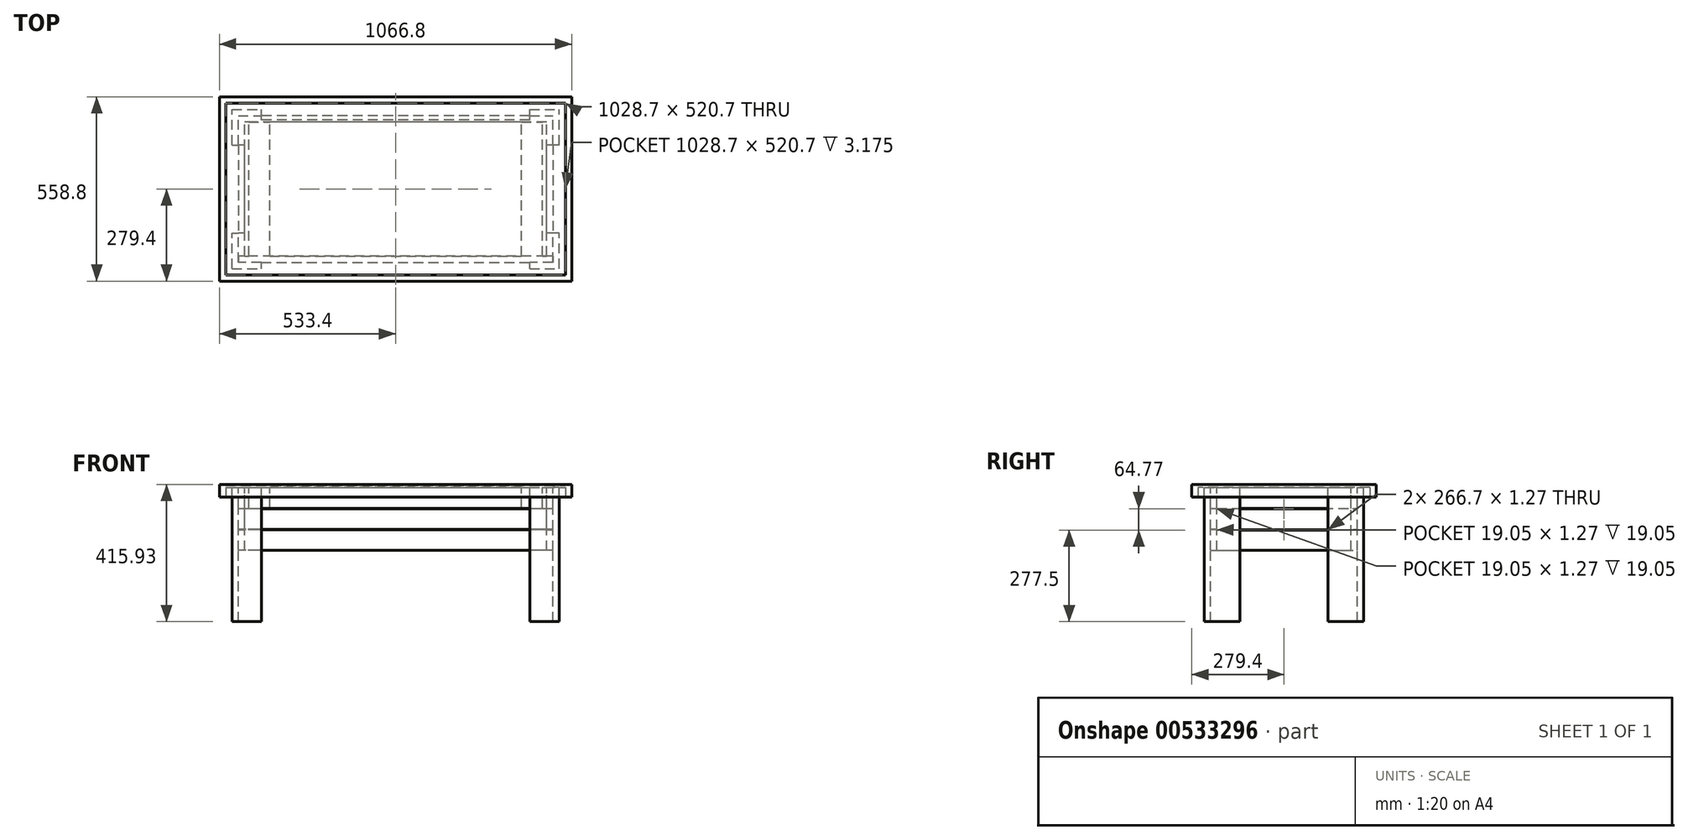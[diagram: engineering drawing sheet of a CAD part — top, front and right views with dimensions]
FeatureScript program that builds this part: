
annotation { "Feature Type Name" : "Feature", "Feature Type Description" : "" }
export const myFeature = defineFeature(function(context is Context, id is Id, definition is map)
    precondition{}
    {
        {
            var Q0;
            Q0=qCreatedBy(makeId("Top.planeOp"),FACE);
            var sketch = newSketch(context, id + "F0", { "sketchPlane" : qUnion([Q0])});
            skLineSegment(sketch, "E0.bottom", {"start": v(-533.4, -279.4) * mm, "end": v(533.4, -279.4) * mm});
            skLineSegment(sketch, "E0.top", {"start": v(-533.4, 279.4) * mm, "end": v(533.4, 279.4) * mm});
            skLineSegment(sketch, "E0.left", {"start": v(-533.4, -279.4) * mm, "end": v(-533.4, 279.4) * mm});
            skLineSegment(sketch, "E0.right", {"start": v(533.4, -279.4) * mm, "end": v(533.4, 279.4) * mm});
            skPoint(sketch, "E0.middle", {"position": v(0, 0) * mm});
            skLineSegment(sketch, "E1.bottom", {"start": v(-514.35, -260.35) * mm, "end": v(514.35, -260.35) * mm});
            skLineSegment(sketch, "E1.top", {"start": v(-514.35, 260.35) * mm, "end": v(514.35, 260.35) * mm});
            skLineSegment(sketch, "E1.left", {"start": v(-514.35, -260.35) * mm, "end": v(-514.35, 260.35) * mm});
            skLineSegment(sketch, "E1.right", {"start": v(514.35, -260.35) * mm, "end": v(514.35, 260.35) * mm});
            skSolve(sketch);
        }
        {
            var Q0;
            Q0=makeQuery(id+"F0.imprint","IMPRINT",FACE,{"disambiguationData":[TD([[makeQuery(id+"F0.imprint","IMPRINT",EDGE,{"derivedFrom":sQuery(id+"F0.wireOp",EDGE,"E0.bottom")}),1.0]])]});
            extrude(context, id + "F1", {"entities" : qUnion([Q0]), "depth" : 38.1 * mm, "offsetDistance" : 25.4 * mm});
        }
        {
            var Q0;
            Q0=makeQuery(id+"F1.opExtrude","SWEPT_FACE",FACE,{"disambiguationData":[OSD([sQuery(id+"F0.wireOp",EDGE,"E1.bottom")])]});
            var sketch = newSketch(context, id + "F2", { "sketchPlane" : qUnion([Q0])});
            skLineSegment(sketch, "E2.bottom", {"start": v(514.35, 34.93) * mm, "end": v(-514.35, 34.92) * mm});
            skLineSegment(sketch, "E2.top", {"start": v(514.35, 28.58) * mm, "end": v(-514.35, 28.57) * mm});
            skLineSegment(sketch, "E2.left", {"start": v(514.35, 34.93) * mm, "end": v(514.35, 28.58) * mm});
            skLineSegment(sketch, "E2.right", {"start": v(-514.35, 34.92) * mm, "end": v(-514.35, 28.57) * mm});
            skSolve(sketch);
        }
        {
            var Q0;
            Q0 = qSketchRegion(id + "F2", true);
            extrude(context, id + "F3", {"entities" : qUnion([Q0]), "operationType" : NewBodyOperationType.ADD, "depth" : 520.7 * mm, "offsetDistance" : 25.4 * mm});
        }
        {
            var Q0;
            Q0=makeQuery(id+"F3.opExtrude","SWEPT_FACE",FACE,{"disambiguationData":[OSD([sQuery(id+"F2.wireOp",EDGE,"E2.top")])]});
            var sketch = newSketch(context, id + "F4", { "sketchPlane" : qUnion([Q0])});
            skLineSegment(sketch, "E3.bottom", {"start": v(-476.25, 222.25) * mm, "end": v(476.25, 222.25) * mm});
            skLineSegment(sketch, "E3.top", {"start": v(-476.25, 203.2) * mm, "end": v(476.25, 203.2) * mm});
            skLineSegment(sketch, "E3.left", {"start": v(-476.25, 222.25) * mm, "end": v(-476.25, 203.2) * mm});
            skLineSegment(sketch, "E3.right", {"start": v(476.25, 222.25) * mm, "end": v(476.25, 203.2) * mm});
            skSolve(sketch);
        }
        {
            var Q0;
            Q0=makeQuery(id+"F4.imprint","IMPRINT",FACE,{"disambiguationData":[TD([[makeQuery(id+"F4.imprint","IMPRINT",EDGE,{"derivedFrom":sQuery(id+"F4.wireOp",EDGE,"E3.bottom")}),-1.0]])]});
            extrude(context, id + "F5", {"entities" : qUnion([Q0]), "operationType" : NewBodyOperationType.ADD, "depth" : 63.5 * mm, "offsetDistance" : 25.4 * mm});
        }
        {
            var Q0;
            Q0=makeQuery(id+"F3.opExtrude","SWEPT_FACE",FACE,{"disambiguationData":[OSD([sQuery(id+"F2.wireOp",EDGE,"E2.top")])]});
            var sketch = newSketch(context, id + "F6", { "sketchPlane" : qUnion([Q0])});
            skLineSegment(sketch, "E4.bottom", {"start": v(-444.5, 203.2) * mm, "end": v(-381, 203.2) * mm});
            skLineSegment(sketch, "E4.top", {"start": v(-444.5, -203.2) * mm, "end": v(-381, -203.2) * mm});
            skLineSegment(sketch, "E4.left", {"start": v(-444.5, 203.2) * mm, "end": v(-444.5, -203.2) * mm});
            skLineSegment(sketch, "E4.right", {"start": v(-381, 203.2) * mm, "end": v(-381, -203.2) * mm});
            skLineSegment(sketch, "E5.bottom", {"start": v(381, 203.2) * mm, "end": v(444.5, 203.2) * mm});
            skLineSegment(sketch, "E5.top", {"start": v(381, -203.2) * mm, "end": v(444.5, -203.2) * mm});
            skLineSegment(sketch, "E5.left", {"start": v(381, 203.2) * mm, "end": v(381, -203.2) * mm});
            skLineSegment(sketch, "E5.right", {"start": v(444.5, 203.2) * mm, "end": v(444.5, -203.2) * mm});
            skSolve(sketch);
        }
        {
            var Q0;
            Q0 = qSketchRegion(id + "F6", true);
            extrude(context, id + "F7", {"entities" : qUnion([Q0]), "operationType" : NewBodyOperationType.ADD, "depth" : 63.5 * mm, "offsetDistance" : 25.4 * mm});
        }
        {
            var Q0;
            Q0=makeQuery(id+"F3.opExtrude","SWEPT_FACE",FACE,{"disambiguationData":[OSD([sQuery(id+"F2.wireOp",EDGE,"E2.top")])]});
            var sketch = newSketch(context, id + "F8", { "sketchPlane" : qUnion([Q0])});
            skLineSegment(sketch, "E6.bottom", {"start": v(-495.3, 241.3) * mm, "end": v(-406.4, 241.3) * mm});
            skLineSegment(sketch, "E6.top", {"start": v(-495.3, 222.25) * mm, "end": v(-406.4, 222.25) * mm});
            skLineSegment(sketch, "E6.left", {"start": v(-495.3, 241.3) * mm, "end": v(-495.3, 222.25) * mm});
            skLineSegment(sketch, "E6.right", {"start": v(-406.4, 241.3) * mm, "end": v(-406.4, 222.25) * mm});
            skLineSegment(sketch, "E7.bottom", {"start": v(-495.3, -222.25) * mm, "end": v(-406.4, -222.25) * mm});
            skLineSegment(sketch, "E7.top", {"start": v(-495.3, -241.3) * mm, "end": v(-406.4, -241.3) * mm});
            skLineSegment(sketch, "E7.left", {"start": v(-495.3, -222.25) * mm, "end": v(-495.3, -241.3) * mm});
            skLineSegment(sketch, "E7.right", {"start": v(-406.4, -222.25) * mm, "end": v(-406.4, -241.3) * mm});
            skLineSegment(sketch, "E8.bottom", {"start": v(406.4, -222.25) * mm, "end": v(495.3, -222.25) * mm});
            skLineSegment(sketch, "E8.top", {"start": v(406.4, -241.3) * mm, "end": v(495.3, -241.3) * mm});
            skLineSegment(sketch, "E8.left", {"start": v(406.4, -222.25) * mm, "end": v(406.4, -241.3) * mm});
            skLineSegment(sketch, "E8.right", {"start": v(495.3, -222.25) * mm, "end": v(495.3, -241.3) * mm});
            skLineSegment(sketch, "E9.bottom", {"start": v(406.4, 241.3) * mm, "end": v(495.3, 241.3) * mm});
            skLineSegment(sketch, "E9.top", {"start": v(406.4, 222.25) * mm, "end": v(495.3, 222.25) * mm});
            skLineSegment(sketch, "E9.left", {"start": v(406.4, 241.3) * mm, "end": v(406.4, 222.25) * mm});
            skLineSegment(sketch, "E9.right", {"start": v(495.3, 241.3) * mm, "end": v(495.3, 222.25) * mm});
            skLineSegment(sketch, "E10.bottom", {"start": v(-495.3, 222.25) * mm, "end": v(-476.25, 222.25) * mm});
            skLineSegment(sketch, "E10.top", {"start": v(-495.3, 133.35) * mm, "end": v(-476.25, 133.35) * mm});
            skLineSegment(sketch, "E10.left", {"start": v(-495.3, 222.25) * mm, "end": v(-495.3, 133.35) * mm});
            skLineSegment(sketch, "E10.right", {"start": v(-476.25, 222.25) * mm, "end": v(-476.25, 133.35) * mm});
            skLineSegment(sketch, "E11.bottom", {"start": v(-495.3, -222.25) * mm, "end": v(-476.25, -222.25) * mm});
            skLineSegment(sketch, "E11.top", {"start": v(-495.3, -133.35) * mm, "end": v(-476.25, -133.35) * mm});
            skLineSegment(sketch, "E11.left", {"start": v(-495.3, -222.25) * mm, "end": v(-495.3, -133.35) * mm});
            skLineSegment(sketch, "E11.right", {"start": v(-476.25, -222.25) * mm, "end": v(-476.25, -133.35) * mm});
            skLineSegment(sketch, "E12.bottom", {"start": v(495.3, 222.25) * mm, "end": v(476.25, 222.25) * mm});
            skLineSegment(sketch, "E12.top", {"start": v(495.3, 133.35) * mm, "end": v(476.25, 133.35) * mm});
            skLineSegment(sketch, "E12.left", {"start": v(495.3, 222.25) * mm, "end": v(495.3, 133.35) * mm});
            skLineSegment(sketch, "E12.right", {"start": v(476.25, 222.25) * mm, "end": v(476.25, 133.35) * mm});
            skLineSegment(sketch, "E13.bottom", {"start": v(495.3, -222.25) * mm, "end": v(476.25, -222.25) * mm});
            skLineSegment(sketch, "E13.top", {"start": v(495.3, -133.35) * mm, "end": v(476.25, -133.35) * mm});
            skLineSegment(sketch, "E13.left", {"start": v(495.3, -222.25) * mm, "end": v(495.3, -133.35) * mm});
            skLineSegment(sketch, "E13.right", {"start": v(476.25, -222.25) * mm, "end": v(476.25, -133.35) * mm});
            skSolve(sketch);
        }
        {
            var Q0;
            Q0 = qSketchRegion(id + "F8", true);
            extrude(context, id + "F9", {"entities" : qUnion([Q0]), "operationType" : NewBodyOperationType.ADD, "depth" : 406.4 * mm, "offsetDistance" : 25.4 * mm});
        }
        {
            var Q0;
            Q0=makeQuery(id+"F3.opExtrude","SWEPT_FACE",FACE,{"disambiguationData":[OSD([sQuery(id+"F2.wireOp",EDGE,"E2.top")])]});
            var sketch = newSketch(context, id + "F10", { "sketchPlane" : qUnion([Q0])});
            skLineSegment(sketch, "E14.bottom", {"start": v(476.25, 203.2) * mm, "end": v(457.2, 203.2) * mm});
            skLineSegment(sketch, "E14.top", {"start": v(476.25, -222.25) * mm, "end": v(457.2, -222.25) * mm});
            skLineSegment(sketch, "E14.left", {"start": v(476.25, 203.2) * mm, "end": v(476.25, -222.25) * mm});
            skLineSegment(sketch, "E14.right", {"start": v(457.2, 203.2) * mm, "end": v(457.2, -222.25) * mm});
            skLineSegment(sketch, "E15.bottom", {"start": v(457.2, -222.25) * mm, "end": v(-457.2, -222.25) * mm});
            skLineSegment(sketch, "E15.top", {"start": v(457.2, -203.2) * mm, "end": v(-457.2, -203.2) * mm});
            skLineSegment(sketch, "E15.left", {"start": v(457.2, -222.25) * mm, "end": v(457.2, -203.2) * mm});
            skLineSegment(sketch, "E15.right", {"start": v(-457.2, -222.25) * mm, "end": v(-457.2, -203.2) * mm});
            skLineSegment(sketch, "E16.bottom", {"start": v(-476.25, 203.2) * mm, "end": v(-457.2, 203.2) * mm});
            skLineSegment(sketch, "E16.top", {"start": v(-476.25, -222.25) * mm, "end": v(-457.2, -222.25) * mm});
            skLineSegment(sketch, "E16.left", {"start": v(-476.25, 203.2) * mm, "end": v(-476.25, -222.25) * mm});
            skLineSegment(sketch, "E16.right", {"start": v(-457.2, 203.2) * mm, "end": v(-457.2, -222.25) * mm});
            skSolve(sketch);
        }
        {
            var Q0;
            Q0 = qSketchRegion(id + "F10", true);
            extrude(context, id + "F11", {"entities" : qUnion([Q0]), "operationType" : NewBodyOperationType.ADD, "depth" : 190.5 * mm, "offsetDistance" : 25.4 * mm});
        }
        {
            var Q0;
            Q0=makeQuery(id+"F11.opExtrude","SWEPT_FACE",FACE,{"disambiguationData":[OSD([sQuery(id+"F10.wireOp",EDGE,"E14.top"),sQuery(id+"F10.wireOp",EDGE,"E15.bottom"),sQuery(id+"F10.wireOp",EDGE,"E16.top")])]});
            var sketch = newSketch(context, id + "F12", { "sketchPlane" : qUnion([Q0])});
            skLineSegment(sketch, "E17.bottom", {"start": v(-406.4, -34.93) * mm, "end": v(406.4, -34.93) * mm});
            skLineSegment(sketch, "E17.top", {"start": v(-406.4, -36.2) * mm, "end": v(406.4, -36.2) * mm});
            skLineSegment(sketch, "E17.left", {"start": v(-406.4, -34.93) * mm, "end": v(-406.4, -36.2) * mm});
            skLineSegment(sketch, "E17.right", {"start": v(406.4, -34.93) * mm, "end": v(406.4, -36.2) * mm});
            skLineSegment(sketch, "E18.bottom", {"start": v(-406.4, -99.7) * mm, "end": v(406.4, -99.7) * mm});
            skLineSegment(sketch, "E18.top", {"start": v(-406.4, -98.43) * mm, "end": v(406.4, -98.43) * mm});
            skLineSegment(sketch, "E18.left", {"start": v(-406.4, -99.7) * mm, "end": v(-406.4, -98.43) * mm});
            skLineSegment(sketch, "E18.right", {"start": v(406.4, -99.7) * mm, "end": v(406.4, -98.43) * mm});
            skSolve(sketch);
        }
        {
            var Q0;
            Q0 = qSketchRegion(id + "F12", true);
            extrude(context, id + "F13", {"entities" : qUnion([Q0]), "operationType" : NewBodyOperationType.REMOVE, "oppositeDirection" : true, "depth" : 12.7 * mm, "offsetDistance" : 25.4 * mm});
        }
        {
            var Q0;
            Q0=makeQuery(id+"F11.opExtrude","SWEPT_FACE",FACE,{"disambiguationData":[OSD([sQuery(id+"F10.wireOp",EDGE,"E16.left")])]});
            var sketch = newSketch(context, id + "F14", { "sketchPlane" : qUnion([Q0])});
            skLineSegment(sketch, "E19.bottom", {"start": v(-133.35, -34.93) * mm, "end": v(133.35, -34.93) * mm});
            skLineSegment(sketch, "E19.top", {"start": v(-133.35, -36.2) * mm, "end": v(133.35, -36.2) * mm});
            skLineSegment(sketch, "E19.left", {"start": v(-133.35, -34.93) * mm, "end": v(-133.35, -36.2) * mm});
            skLineSegment(sketch, "E19.right", {"start": v(133.35, -34.93) * mm, "end": v(133.35, -36.2) * mm});
            skLineSegment(sketch, "E20.bottom", {"start": v(-133.35, -99.7) * mm, "end": v(133.35, -99.7) * mm});
            skLineSegment(sketch, "E20.top", {"start": v(-133.35, -100.97) * mm, "end": v(133.35, -100.97) * mm});
            skLineSegment(sketch, "E20.left", {"start": v(-133.35, -99.7) * mm, "end": v(-133.35, -100.97) * mm});
            skLineSegment(sketch, "E20.right", {"start": v(133.35, -99.7) * mm, "end": v(133.35, -100.97) * mm});
            skSolve(sketch);
        }
        {
            var Q0;
            Q0 = qSketchRegion(id + "F14", true);
            extrude(context, id + "F15", {"entities" : qUnion([Q0]), "operationType" : NewBodyOperationType.REMOVE, "oppositeDirection" : true, "depth" : 952.5 * mm, "offsetDistance" : 25.4 * mm});
        }
        {
            var Q0;
            Q0=makeQuery(id+"F9.opExtrude","SWEPT_FACE",FACE,{"disambiguationData":[OSD([sQuery(id+"F8.wireOp",EDGE,"E10.right")])]});
            var sketch = newSketch(context, id + "F16", { "sketchPlane" : qUnion([Q0])});
            skLineSegment(sketch, "E21.bottom", {"start": v(-203.2, -161.93) * mm, "end": v(-222.25, -161.93) * mm});
            skLineSegment(sketch, "E21.top", {"start": v(-203.2, -99.7) * mm, "end": v(-222.25, -99.7) * mm});
            skLineSegment(sketch, "E21.left", {"start": v(-203.2, -161.93) * mm, "end": v(-203.2, -99.7) * mm});
            skLineSegment(sketch, "E21.right", {"start": v(-222.25, -161.93) * mm, "end": v(-222.25, -99.7) * mm});
            skLineSegment(sketch, "E22.bottom", {"start": v(-203.2, -98.43) * mm, "end": v(-222.25, -98.43) * mm});
            skLineSegment(sketch, "E22.top", {"start": v(-203.2, -36.2) * mm, "end": v(-222.25, -36.2) * mm});
            skLineSegment(sketch, "E22.left", {"start": v(-203.2, -98.43) * mm, "end": v(-203.2, -36.2) * mm});
            skLineSegment(sketch, "E22.right", {"start": v(-222.25, -98.43) * mm, "end": v(-222.25, -36.2) * mm});
            skSolve(sketch);
        }
        {
            var Q0;
            Q0 = qSketchRegion(id + "F16", true);
            extrude(context, id + "F17", {"entities" : qUnion([Q0]), "operationType" : NewBodyOperationType.ADD, "depth" : 952.5 * mm, "offsetDistance" : 25.4 * mm});
        }
    });
